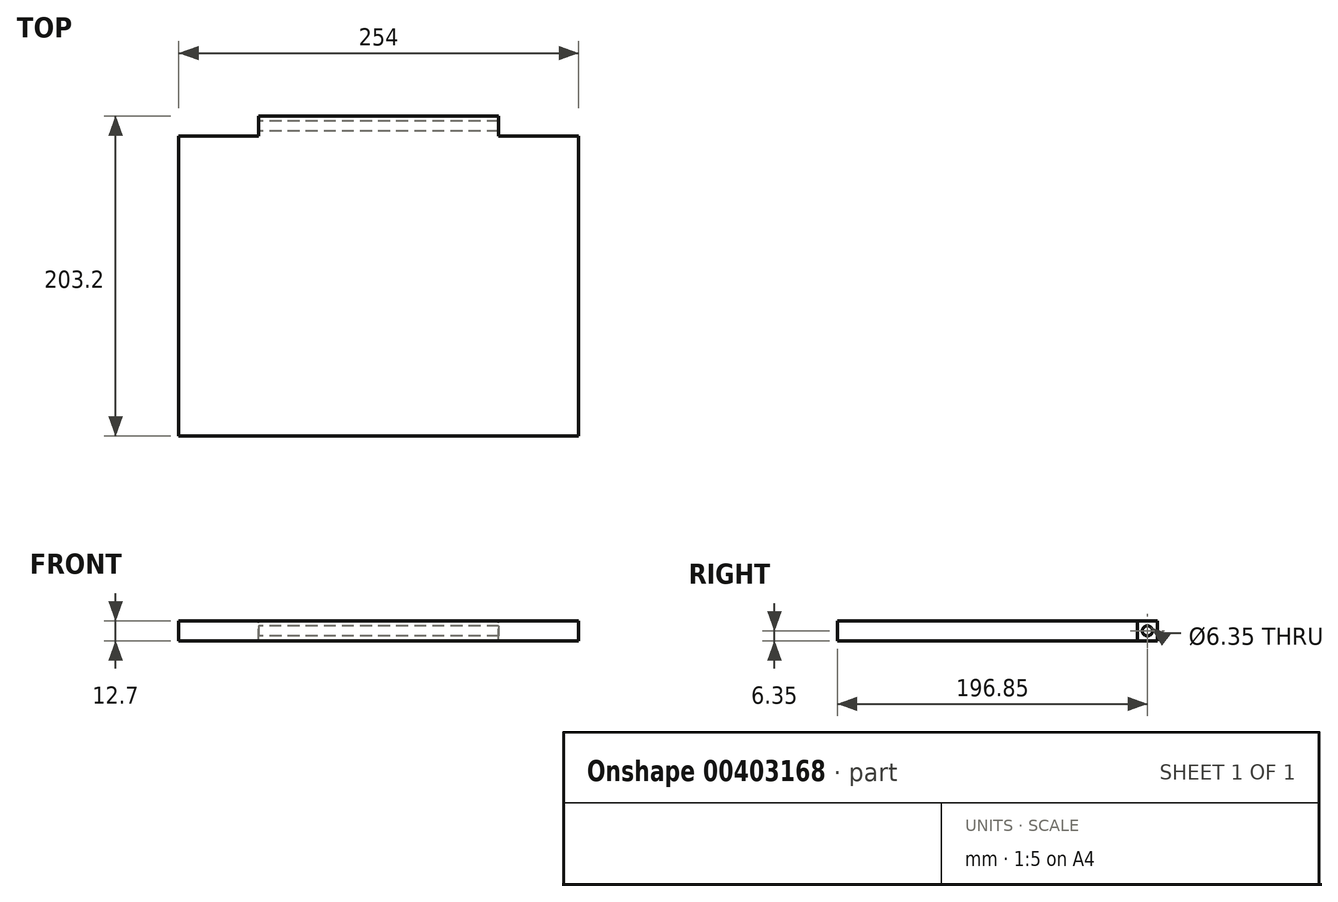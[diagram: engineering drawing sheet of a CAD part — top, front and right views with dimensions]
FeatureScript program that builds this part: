
annotation { "Feature Type Name" : "Feature", "Feature Type Description" : "" }
export const myFeature = defineFeature(function(context is Context, id is Id, definition is map)
    precondition{}
    {
        {
            var Q0;
            Q0=qCreatedBy(makeId("Top.planeOp"),FACE);
            var sketch = newSketch(context, id + "F0", { "sketchPlane" : qUnion([Q0])});
            skLineSegment(sketch, "E0.bottom", {"start": v(-127, 101.6) * mm, "end": v(127, 101.6) * mm});
            skLineSegment(sketch, "E0.top", {"start": v(-127, -101.6) * mm, "end": v(127, -101.6) * mm});
            skLineSegment(sketch, "E0.left", {"start": v(-127, 101.6) * mm, "end": v(-127, -101.6) * mm});
            skLineSegment(sketch, "E0.right", {"start": v(127, 101.6) * mm, "end": v(127, -101.6) * mm});
            skPoint(sketch, "E0.middle", {"position": v(0, 0) * mm});
            skSolve(sketch);
        }
        {
            var Q0;
            Q0=makeQuery(id+"F0.imprint","IMPRINT",FACE,{"disambiguationData":[TD([[makeQuery(id+"F0.imprint","IMPRINT",EDGE,{"derivedFrom":sQuery(id+"F0.wireOp",EDGE,"E0.bottom")}),-1.0]])]});
            extrude(context, id + "F1", {"entities" : qUnion([Q0]), "depth" : 12.7 * mm});
        }
        {
            var Q0;
            Q0=makeQuery(id+"F1.opExtrude","CAP_FACE",FACE,{"disambiguationData":[OSD([sQuery(id+"F0.wireOp",EDGE,"E0.bottom"),sQuery(id+"F0.wireOp",EDGE,"E0.top"),sQuery(id+"F0.wireOp",EDGE,"E0.left"),sQuery(id+"F0.wireOp",EDGE,"E0.right")])],"isStart":false});
            var sketch = newSketch(context, id + "F2", { "sketchPlane" : qUnion([Q0])});
            skLineSegment(sketch, "E1.bottom", {"start": v(-76.2, 101.6) * mm, "end": v(-127, 101.6) * mm});
            skLineSegment(sketch, "E1.top", {"start": v(-76.2, 88.9) * mm, "end": v(-127, 88.9) * mm});
            skLineSegment(sketch, "E1.left", {"start": v(-76.2, 101.6) * mm, "end": v(-76.2, 88.9) * mm});
            skLineSegment(sketch, "E1.right", {"start": v(-127, 101.6) * mm, "end": v(-127, 88.9) * mm});
            skLineSegment(sketch, "E2", {"start": v(0, 101.6) * mm, "end": v(0, -101.6) * mm});
            skLineSegment(sketch, "E3.MirrorCS", {"start": v(127, 101.6) * mm, "end": v(127, 88.9) * mm});
            skLineSegment(sketch, "E4.MirrorCS", {"start": v(76.2, 101.6) * mm, "end": v(76.2, 88.9) * mm});
            skLineSegment(sketch, "E5.MirrorCS", {"start": v(76.2, 88.9) * mm, "end": v(127, 88.9) * mm});
            skLineSegment(sketch, "E6.MirrorCS", {"start": v(76.2, 101.6) * mm, "end": v(127, 101.6) * mm});
            skLineSegment(sketch, "E7", {"start": v(-76.2, 88.9) * mm, "end": v(76.2, 88.9) * mm});
            skLineSegment(sketch, "E8", {"start": v(76.2, 101.6) * mm, "end": v(-76.2, 101.6) * mm});
            skSolve(sketch);
        }
        {
            var Q0;
            Q0=makeQuery(id+"F1.opExtrude","SWEPT_FACE",FACE,{"disambiguationData":[OSD([sQuery(id+"F0.wireOp",EDGE,"E0.left")])]});
            var sketch = newSketch(context, id + "F3", { "sketchPlane" : qUnion([Q0])});
            skLineSegment(sketch, "E9", {"start": v(-101.6, 6.35) * mm, "end": v(-86.85, 6.35) * mm});
            skCircle(sketch, "E10", {"center": v(-95.25, 6.35) * mm, "radius": 3.18 * mm});
            skSolve(sketch);
        }
        {
            var Q0;
            Q0 = qSketchRegion(id + "F3", true);
            extrude(context, id + "F4", {"entities" : qUnion([Q0]), "operationType" : NewBodyOperationType.REMOVE, "endBound" : BoundingType.THROUGH_ALL, "oppositeDirection" : true, "depth" : 25.4 * mm});
        }
        {
            var Q0;
            Q0=makeQuery(id+"F2.imprint","IMPRINT",FACE,{"disambiguationData":[TD([[makeQuery(id+"F2.imprint","IMPRINT",EDGE,{"derivedFrom":sQuery(id+"F2.wireOp",EDGE,"E1.bottom")}),-1.0]])]});
            var Q1;
            Q1=makeQuery(id+"F2.imprint","IMPRINT",FACE,{"disambiguationData":[TD([[makeQuery(id+"F2.imprint","IMPRINT",EDGE,{"derivedFrom":sQuery(id+"F2.wireOp",EDGE,"E3.MirrorCS")}),-1.0]])]});
            extrude(context, id + "F5", {"entities" : qUnion([Q0, Q1]), "operationType" : NewBodyOperationType.REMOVE, "endBound" : BoundingType.THROUGH_ALL, "oppositeDirection" : true, "depth" : 25.4 * mm});
        }
    });
